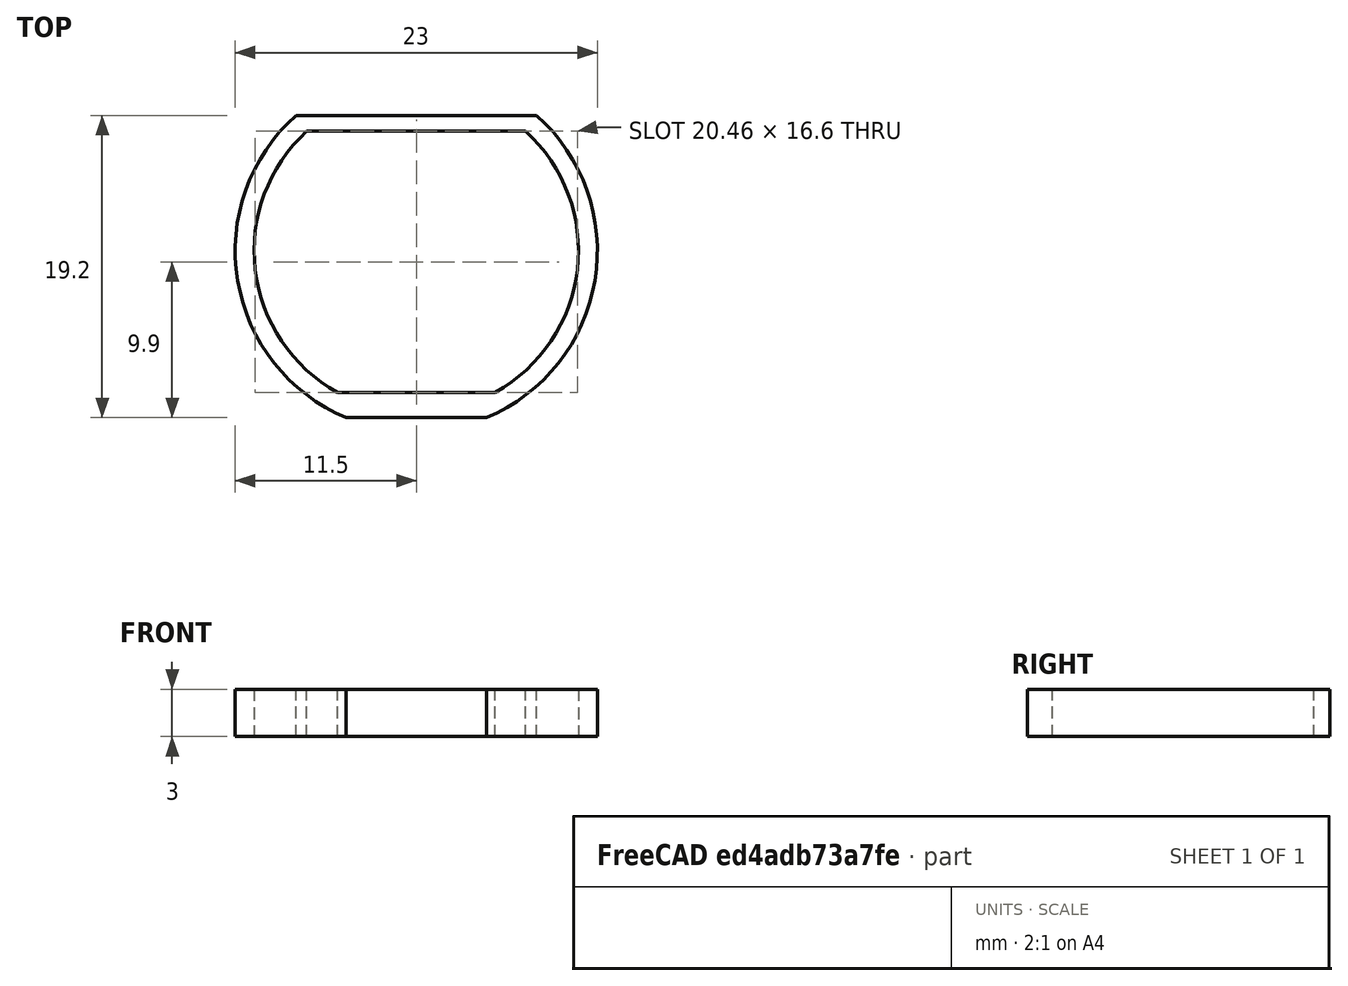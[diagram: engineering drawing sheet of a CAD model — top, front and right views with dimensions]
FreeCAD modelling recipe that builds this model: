
FCSTD DOCUMENT  (FreeCAD 0.17R13541 (Git))
Label: motor_strain_relief
License: All rights reserved
LicenseURL: http://en.wikipedia.org/wiki/All_rights_reserved
objects: Sketcher::SketchObject×1, PartDesign::Pad×1, PartDesign::Body×1
note: 4 computed .brp shape members not serialized (recipe doc carries the construction recipe); baked Part::Feature solids carry a one-line shape summary decoded from their .brp

FEATURE [Sketcher::SketchObject] Sketch
  MapMode = 5
  Support = -> [XY_Plane]
  sketch-geometry (8):
    g0: ArcOfCircle CenterX=0 CenterY=0 CenterZ=0 NormalX=0 NormalY=0 NormalZ=1 AngleXU=0 Radius=10.3 StartAngle=2.31169 EndAngle=4.20453
    g1: ArcOfCircle CenterX=0 CenterY=0 CenterZ=0 NormalX=0 NormalY=0 NormalZ=1 AngleXU=0 Radius=10.3 StartAngle=5.22025 EndAngle=7.11309
    g2: LineSegment StartX=-6.95198 StartY=7.6 StartZ=0 EndX=6.95198 EndY=7.6 EndZ=0
    g3: LineSegment StartX=-5.00899 StartY=-9 StartZ=0 EndX=5.00899 EndY=-9 EndZ=0
    g4: LineSegment StartX=-7.63479 StartY=8.6 StartZ=0 EndX=7.63479 EndY=8.6 EndZ=0
    g5: LineSegment StartX=4.45982 StartY=-10.6 StartZ=0 EndX=-4.45982 EndY=-10.6 EndZ=0
    g6: ArcOfCircle CenterX=0 CenterY=0 CenterZ=0 NormalX=0 NormalY=0 NormalZ=1 AngleXU=0 Radius=11.5 StartAngle=2.29681 EndAngle=4.31413
    g7: ArcOfCircle CenterX=0 CenterY=0 CenterZ=0 NormalX=0 NormalY=0 NormalZ=1 AngleXU=0 Radius=11.5 StartAngle=5.11064 EndAngle=7.12797
  constraints (24):
    c: Coincident(g0,g-1)
    c: Coincident(g1,g-1)
    c: Coincident(g2,g0)
    c: Coincident(g2,g1)
    c: Horizontal(g2)
    c: Coincident(g3,g0)
    c: Coincident(g3,g1)
    c: Horizontal(g3)
    c: Equal(g1,g0)
    c: Radius(g1) = 10.3
    c: Horizontal(g4)
    c: Horizontal(g5)
    c: DistanceY(g1,g4) = 1
    c: Coincident(g6,g-1)
    c: Coincident(g6,g4)
    c: Coincident(g6,g5)
    c: Coincident(g7,g-1)
    c: Coincident(g7,g4)
    c: Coincident(g7,g5)
    c: Equal(g7,g6)
    c: Radius(g7) = 11.5
    c: DistanceY(g-1,g0) = 7.6
    c: DistanceY(g1,g-1) = 9
    c: DistanceY(g5,g-1) = 10.6
FEATURE [PartDesign::Pad] Pad
  Length = 3
  Length2 = 100
  Profile = -> Sketch
  Type = 0
FEATURE [PartDesign::Body] Body
  Group = -> [Sketch,Pad]
  Origin = -> Origin
  Tip = -> Pad
